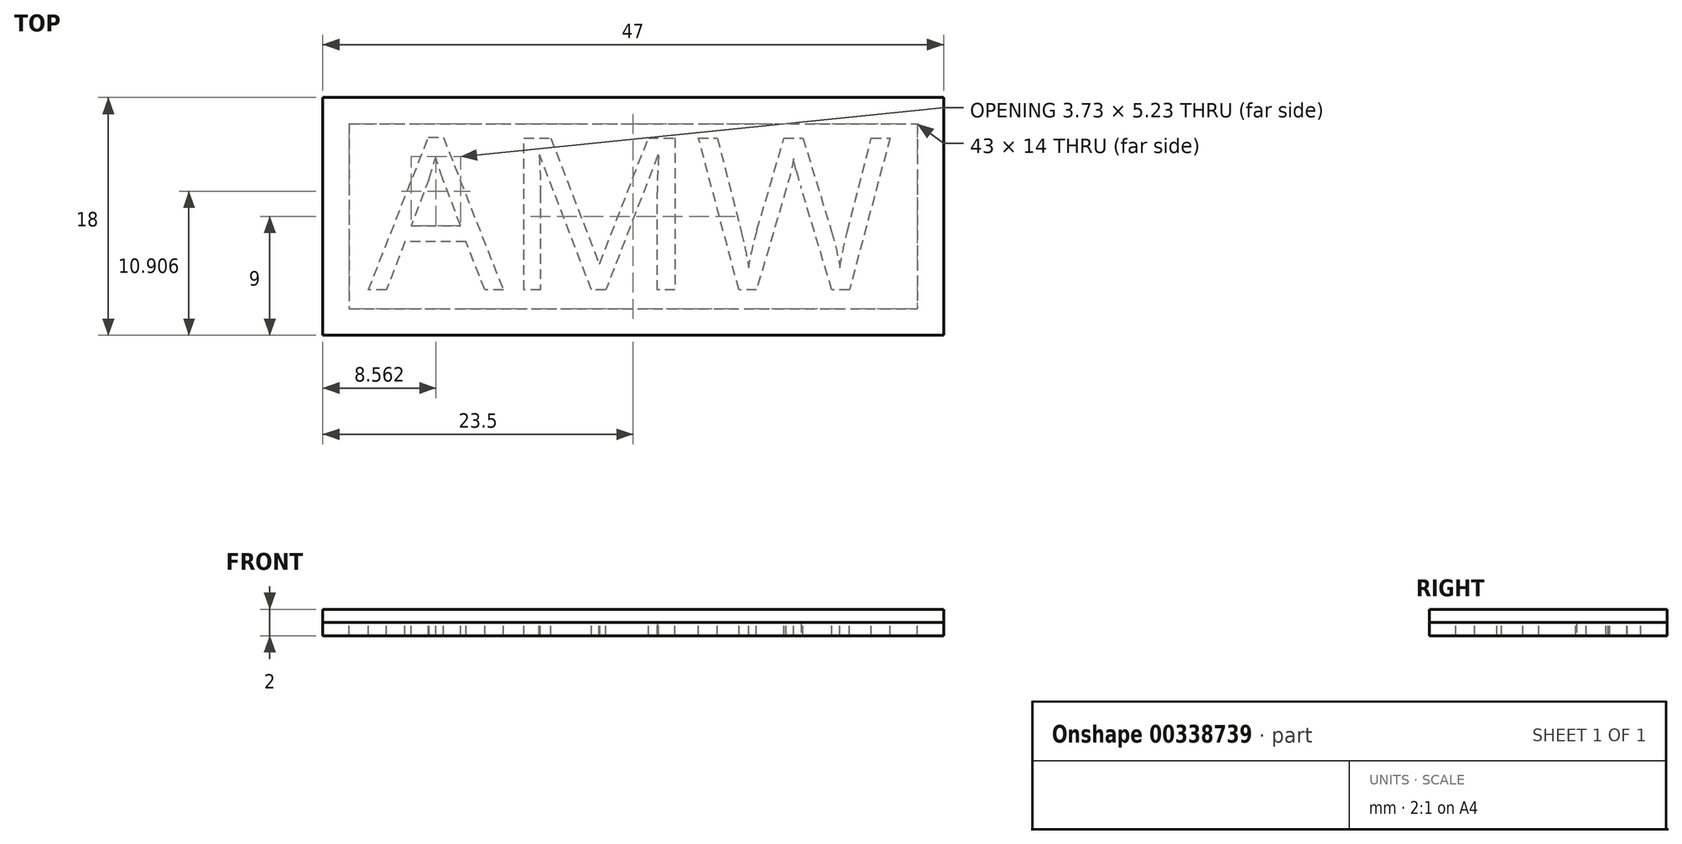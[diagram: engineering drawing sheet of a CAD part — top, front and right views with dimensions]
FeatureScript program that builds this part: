
annotation { "Feature Type Name" : "Feature", "Feature Type Description" : "" }
export const myFeature = defineFeature(function(context is Context, id is Id, definition is map)
    precondition{}
    {
        {
            var Q0;
            Q0=qCreatedBy(makeId("Top.planeOp"),FACE);
            var sketch = newSketch(context, id + "F0", { "sketchPlane" : qUnion([Q0])});
            skLineSegment(sketch, "E0.bottom", {"start": v(-23.5, 9) * mm, "end": v(23.5, 9) * mm});
            skLineSegment(sketch, "E0.top", {"start": v(-23.5, -9) * mm, "end": v(23.5, -9) * mm});
            skLineSegment(sketch, "E0.left", {"start": v(-23.5, 9) * mm, "end": v(-23.5, -9) * mm});
            skLineSegment(sketch, "E0.right", {"start": v(23.5, 9) * mm, "end": v(23.5, -9) * mm});
            skPoint(sketch, "E0.middle", {"position": v(0, 0) * mm});
            skLineSegment(sketch, "E1.0", {"start": v(-21.5, 7) * mm, "end": v(-21.5, -9) * mm});
            skLineSegment(sketch, "E1.1", {"start": v(-21.5, 7) * mm, "end": v(23.5, 7) * mm});
            skLineSegment(sketch, "E2.0", {"start": v(21.5, 9) * mm, "end": v(21.5, -7) * mm});
            skLineSegment(sketch, "E2.1", {"start": v(-23.5, -7) * mm, "end": v(21.5, -7) * mm});
            skSolve(sketch);
        }
        {
            var Q0;
            {var subQ0=sQuery(id+"F0.wireOp",EDGE,"E0.right");var subQ1=sQuery(id+"F0.wireOp",EDGE,"E0.bottom");var subQ2=makeQuery(id+"F0.imprint","INTERSECT",VERTEX,{"derivedFrom":[subQ1,subQ0]});Q0=makeQuery(id+"F0.imprint","IMPRINT",FACE,{"disambiguationData":[TD([[makeQuery(id+"F0.imprint","IMPRINT",EDGE,{"disambiguationData":[TD([[subQ2,1.0]])],"derivedFrom":subQ1}),-1.0]])]});}
            var Q1;
            {var subQ0=sQuery(id+"F0.wireOp",EDGE,"E0.left");var subQ1=sQuery(id+"F0.wireOp",EDGE,"E0.top");var subQ2=makeQuery(id+"F0.imprint","INTERSECT",VERTEX,{"derivedFrom":[subQ1,subQ0]});Q1=makeQuery(id+"F0.imprint","IMPRINT",FACE,{"disambiguationData":[TD([[makeQuery(id+"F0.imprint","IMPRINT",EDGE,{"disambiguationData":[TD([[subQ2,-1.0]])],"derivedFrom":subQ1}),1.0]])]});}
            var Q2;
            {var subQ1=sQuery(id+"F0.wireOp",EDGE,"E0.right");var subQ6=sQuery(id+"F0.wireOp",EDGE,"E0.top");var subQ10=makeQuery(id+"F0.imprint","INTERSECT",VERTEX,{"derivedFrom":[subQ6,subQ1]});Q2=makeQuery(id+"F0.imprint","IMPRINT",FACE,{"disambiguationData":[TD([[makeQuery(id+"F0.imprint","IMPRINT",EDGE,{"disambiguationData":[TD([[subQ10,1.0]])],"derivedFrom":subQ6}),1.0]])]});}
            var Q3;
            {var subQ5=sQuery(id+"F0.wireOp",EDGE,"E0.left");var subQ6=sQuery(id+"F0.wireOp",EDGE,"E0.bottom");var subQ7=makeQuery(id+"F0.imprint","INTERSECT",VERTEX,{"derivedFrom":[subQ6,subQ5]});Q3=makeQuery(id+"F0.imprint","IMPRINT",FACE,{"disambiguationData":[TD([[makeQuery(id+"F0.imprint","IMPRINT",EDGE,{"disambiguationData":[TD([[subQ7,-1.0]])],"derivedFrom":subQ6}),-1.0]])]});}
            extrude(context, id + "F1", {"entities" : qUnion([Q0, Q1, Q2, Q3]), "oppositeDirection" : true, "depth" : 1 * mm});
        }
        {
            var Q0;
            Q0=qCreatedBy(makeId("Top.planeOp"),FACE);
            var sketch = newSketch(context, id + "F2", { "sketchPlane" : qUnion([Q0])});
            skText(sketch, "E3", { "text": "AMW", "fontName": "OpenSans-Regular.ttf"});
            const initialGuessF2  = {"E3": [-0.02005, -0.00558, 1, 0, 0.01162]};
            skSetInitialGuess(sketch, initialGuessF2);
            skSolve(sketch);
        }
        {
            var Q0;
            Q0 = qSketchRegion(id + "F2", true);
            extrude(context, id + "F3", {"entities" : qUnion([Q0]), "oppositeDirection" : true, "depth" : 1 * mm});
        }
        {
            var Q0;
            Q0=qCreatedBy(makeId("Top.planeOp"),FACE);
            var sketch = newSketch(context, id + "F4", { "sketchPlane" : qUnion([Q0])});
            skLineSegment(sketch, "E4.bottom", {"start": v(-23.5, 9) * mm, "end": v(23.5, 9) * mm});
            skLineSegment(sketch, "E4.top", {"start": v(-23.5, -9) * mm, "end": v(23.5, -9) * mm});
            skLineSegment(sketch, "E4.left", {"start": v(-23.5, 9) * mm, "end": v(-23.5, -9) * mm});
            skLineSegment(sketch, "E4.right", {"start": v(23.5, 9) * mm, "end": v(23.5, -9) * mm});
            skPoint(sketch, "E4.middle", {"position": v(0, 0) * mm});
            skSolve(sketch);
        }
        {
            var Q0;
            Q0 = qSketchRegion(id + "F4", true);
            extrude(context, id + "F5", {"entities" : qUnion([Q0]), "depth" : 1 * mm});
        }
    });
